# Revit family: Single Handle Lavatory Faucet without pop-up waste_TOTO_TLS03304
name_source: partatom
category: 衛生器具
revit_build: Autodesk Revit 2018 (Build: 20170223_1515(x64)
units: mm (PartAtom-declared; Revit-internal decimal feet)

## family parameters
OmniClass タイトル = Sanitary, Laundry, and Cleaning Equipment
OmniClass 番号 = 23.45.00.00
パーツ タイプ = 標準
ロード時にボイドで切り取り = いいえ
丸型コネクタ寸法 = 直径を使用
作業面ベース = いいえ
共有 = いいえ
常に垂直 = はい
部屋計算ポイント = いいえ

## types (1)
- Single Handle Lavatory Faucet without pop-up waste_TOTO_TLS03304
    Finish = faucet_material
    Height = 258
    Length = 133.8
    TOTO AsiaOceania = TLS03304B
    TOTO AsiaOceania URL = http://asia.toto.com
    TOTO China = TLS03304B
    TOTO China URL = http://www.toto.com.cn
    TOTO India = TLS03304B
    TOTO India URL = https://in.toto.com
    TOTO Taiwan = TLS03304PA
    TOTO Taiwan URL = https://www.twtoto.com.tw
    TOTO Thailand = TLS03304T
    TOTO Thailand URL = https://th.toto.com
    Width = 47
    タイプの説明 = for Semi-tall Vessel
    モデル = TLS03304
    製造元 = TOTO Ltd.
    説明 = Single Handle Lavatory Faucet without pop-up waste/单柄双控洗面器水嘴

## geometry (parser evidence)
native form markers: Sweep x2
no freeform markers — native parametric forms only
